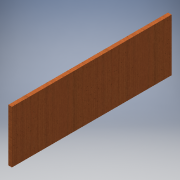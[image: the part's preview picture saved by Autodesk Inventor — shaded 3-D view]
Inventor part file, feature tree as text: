
AUTODESK INVENTOR PART (.ipt)
format: ipt  version: 2016 (Build 200138000, 138)  size: 104,448 bytes
history: native  units: in
note: dims shown in document units (in); Inventor stores cm internally (conversion verified against a paired STEP export)
features: extrude x1, sketch x1
ambient origin geometry x8: Origin, YZ Plane, XZ Plane, XY Plane, X Axis, Y Axis, Z Axis, Center Point
bodies: Solid1 (feature_tree)
feature tree (2):
  extrude  "Extrusion1"  Depth=6.5in
  sketch  "Sketch1"  dims[d0=19.75in d1=6.5in d2=0.4375in d3=0.0in]
